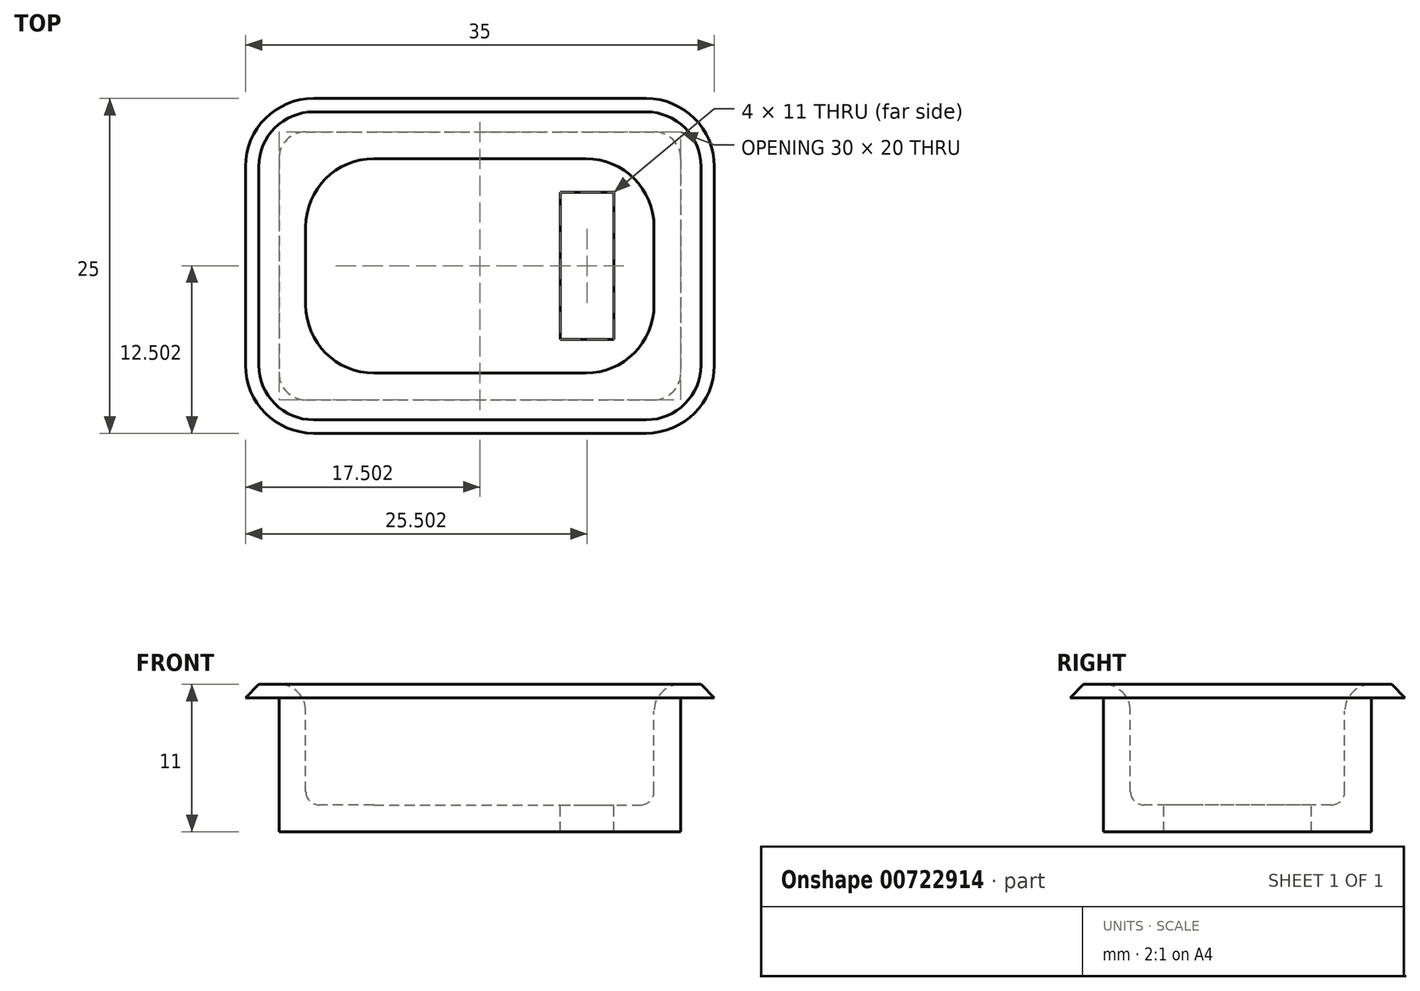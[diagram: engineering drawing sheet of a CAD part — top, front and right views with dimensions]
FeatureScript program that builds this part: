
annotation { "Feature Type Name" : "Feature", "Feature Type Description" : "" }
export const myFeature = defineFeature(function(context is Context, id is Id, definition is map)
    precondition{}
    {
        {
            var Q0;
            Q0=qCreatedBy(makeId("Top.planeOp"),FACE);
            var sketch = newSketch(context, id + "F0", { "sketchPlane" : qUnion([Q0])});
            skLineSegment(sketch, "E0.bottom", {"start": v(-34.97, -17.82) * mm, "end": v(-4.97, -17.82) * mm});
            skLineSegment(sketch, "E0.top", {"start": v(-34.97, -37.82) * mm, "end": v(-4.97, -37.82) * mm});
            skLineSegment(sketch, "E0.left", {"start": v(-34.97, -17.82) * mm, "end": v(-34.97, -37.82) * mm});
            skLineSegment(sketch, "E0.right", {"start": v(-4.97, -17.82) * mm, "end": v(-4.97, -37.82) * mm});
            skSolve(sketch);
        }
        {
            var Q0;
            Q0=makeQuery(id+"F0.imprint","IMPRINT",FACE,{"disambiguationData":[TD([[makeQuery(id+"F0.imprint","IMPRINT",EDGE,{"derivedFrom":sQuery(id+"F0.wireOp",EDGE,"E0.bottom")}),-1.0]])]});
            extrude(context, id + "F1", {"entities" : qUnion([Q0]), "depth" : 10 * mm, "offsetDistance" : 25.4 * mm});
        }
        {
            var Q0;
            Q0=makeQuery(id+"F1.opExtrude","SWEPT_EDGE",EDGE,{"disambiguationData":[OSD([sQuery(id+"F0.wireOp",EDGE,"E0.top"),sQuery(id+"F0.wireOp",EDGE,"E0.right")])]});
            var Q1;
            Q1=makeQuery(id+"F1.opExtrude","SWEPT_EDGE",EDGE,{"disambiguationData":[OSD([sQuery(id+"F0.wireOp",EDGE,"E0.bottom"),sQuery(id+"F0.wireOp",EDGE,"E0.right")])]});
            var Q2;
            Q2=makeQuery(id+"F1.opExtrude","SWEPT_EDGE",EDGE,{"disambiguationData":[OSD([sQuery(id+"F0.wireOp",EDGE,"E0.top"),sQuery(id+"F0.wireOp",EDGE,"E0.left")])]});
            var Q3;
            Q3=makeQuery(id+"F1.opExtrude","SWEPT_EDGE",EDGE,{"disambiguationData":[OSD([sQuery(id+"F0.wireOp",EDGE,"E0.bottom"),sQuery(id+"F0.wireOp",EDGE,"E0.left")])]});
            fillet(context, id + "F2", {"entities" : qUnion([Q0, Q1, Q2, Q3]), "radius" : 2 * mm, "tangentPropagation" : true, "allowEdgeOverflow" : false});
        }
        {
            var Q0;
            Q0=makeQuery(id+"F1.opExtrude","CAP_FACE",FACE,{"disambiguationData":[OSD([sQuery(id+"F0.wireOp",EDGE,"E0.bottom"),sQuery(id+"F0.wireOp",EDGE,"E0.top"),sQuery(id+"F0.wireOp",EDGE,"E0.left"),sQuery(id+"F0.wireOp",EDGE,"E0.right")])],"isStart":false});
            shell(context, id + "F3", {"entities" : qUnion([Q0]), "thickness" : 2 * mm});
        }
        {
            var Q0;
            Q0=makeQuery(id+"F3.opShell","OFFSET_FACE",FACE,{"disambiguationData":[OSD([sQuery(id+"F0.wireOp",EDGE,"E0.bottom"),sQuery(id+"F0.wireOp",EDGE,"E0.top"),sQuery(id+"F0.wireOp",EDGE,"E0.left"),sQuery(id+"F0.wireOp",EDGE,"E0.right")])]});
            var sketch = newSketch(context, id + "F4", { "sketchPlane" : qUnion([Q0])});
            skLineSegment(sketch, "E1.bottom", {"start": v(-13.97, -22.32) * mm, "end": v(-9.97, -22.32) * mm});
            skLineSegment(sketch, "E1.top", {"start": v(-13.97, -33.32) * mm, "end": v(-9.97, -33.32) * mm});
            skLineSegment(sketch, "E1.left", {"start": v(-13.97, -22.32) * mm, "end": v(-13.97, -33.32) * mm});
            skLineSegment(sketch, "E1.right", {"start": v(-9.97, -22.32) * mm, "end": v(-9.97, -33.32) * mm});
            skSolve(sketch);
        }
        {
            var Q0;
            Q0=makeQuery(id+"F4.imprint","IMPRINT",FACE,{"disambiguationData":[TD([[makeQuery(id+"F4.imprint","IMPRINT",EDGE,{"derivedFrom":sQuery(id+"F4.wireOp",EDGE,"E1.bottom")}),-1.0]])]});
            extrude(context, id + "F5", {"entities" : qUnion([Q0]), "operationType" : NewBodyOperationType.REMOVE, "endBound" : BoundingType.THROUGH_ALL, "oppositeDirection" : true, "depth" : 25.4 * mm, "offsetDistance" : 25.4 * mm});
        }
        {
            var Q0;
            Q0=makeQuery(id+"F1.opExtrude","CAP_FACE",FACE,{"disambiguationData":[OSD([sQuery(id+"F0.wireOp",EDGE,"E0.bottom"),sQuery(id+"F0.wireOp",EDGE,"E0.top"),sQuery(id+"F0.wireOp",EDGE,"E0.left"),sQuery(id+"F0.wireOp",EDGE,"E0.right")])],"isStart":false});
            var sketch = newSketch(context, id + "F6", { "sketchPlane" : qUnion([Q0])});
            skLineSegment(sketch, "E2.bottom", {"start": v(-32.97, -19.82) * mm, "end": v(-6.97, -19.82) * mm});
            skLineSegment(sketch, "E2.top", {"start": v(-32.97, -35.82) * mm, "end": v(-6.97, -35.82) * mm});
            skLineSegment(sketch, "E2.left", {"start": v(-32.97, -19.82) * mm, "end": v(-32.97, -35.82) * mm});
            skLineSegment(sketch, "E2.right", {"start": v(-6.97, -19.82) * mm, "end": v(-6.97, -35.82) * mm});
            skLineSegment(sketch, "E3.bottom", {"start": v(-37.47, -15.32) * mm, "end": v(-2.47, -15.32) * mm});
            skLineSegment(sketch, "E3.top", {"start": v(-37.47, -40.32) * mm, "end": v(-2.47, -40.32) * mm});
            skLineSegment(sketch, "E3.left", {"start": v(-37.47, -15.32) * mm, "end": v(-37.47, -40.32) * mm});
            skLineSegment(sketch, "E3.right", {"start": v(-2.47, -15.32) * mm, "end": v(-2.47, -40.32) * mm});
            skSolve(sketch);
        }
        {
            var Q0;
            Q0=makeQuery(id+"F6.imprint","IMPRINT",FACE,{"disambiguationData":[TD([[makeQuery(id+"F6.imprint","IMPRINT",EDGE,{"derivedFrom":sQuery(id+"F6.wireOp",EDGE,"E3.bottom")}),-1.0]])]});
            var Q1;
            Q1=makeQuery(id+"F6.imprint","IMPRINT",FACE,{"disambiguationData":[TD([[makeQuery(id+"F6.imprint","IMPRINT",EDGE,{"derivedFrom":sQuery(id+"F6.wireOp",EDGE,"E2.bottom")}),1.0]])]});
            extrude(context, id + "F7", {"entities" : qUnion([Q0, Q1]), "operationType" : NewBodyOperationType.ADD, "depth" : 1 * mm, "offsetDistance" : 25.4 * mm});
        }
        {
            var Q0;
            Q0=makeQuery(id+"F7.opExtrude","SWEPT_EDGE",EDGE,{"disambiguationData":[OSD([sQuery(id+"F6.wireOp",EDGE,"E3.top"),sQuery(id+"F6.wireOp",EDGE,"E3.right")])]});
            var Q1;
            Q1=makeQuery(id+"F7.opExtrude","SWEPT_EDGE",EDGE,{"disambiguationData":[OSD([sQuery(id+"F6.wireOp",EDGE,"E3.top"),sQuery(id+"F6.wireOp",EDGE,"E3.left")])]});
            var Q2;
            Q2=makeQuery(id+"F7.opExtrude","SWEPT_EDGE",EDGE,{"disambiguationData":[OSD([sQuery(id+"F6.wireOp",EDGE,"E3.bottom"),sQuery(id+"F6.wireOp",EDGE,"E3.right")])]});
            var Q3;
            Q3=makeQuery(id+"F7.opExtrude","SWEPT_EDGE",EDGE,{"disambiguationData":[OSD([sQuery(id+"F6.wireOp",EDGE,"E3.bottom"),sQuery(id+"F6.wireOp",EDGE,"E3.left")])]});
            fillet(context, id + "F8", {"entities" : qUnion([Q0, Q1, Q2, Q3]), "radius" : 5.08 * mm, "tangentPropagation" : true, "allowEdgeOverflow" : false});
        }
        {
            var Q0;
            Q0=makeQuery(id+"F7.boolean.opBoolean","MERGE",EDGE,{"derivedFrom":[makeQuery(id+"F3.opShell","OFFSET_EDGE",EDGE,{"disambiguationData":[OSD([sQuery(id+"F0.wireOp",EDGE,"E0.top"),sQuery(id+"F0.wireOp",EDGE,"E0.right")])]}),makeQuery(id+"F7.opExtrude","SWEPT_EDGE",EDGE,{"disambiguationData":[OSD([sQuery(id+"F6.wireOp",EDGE,"E2.top"),sQuery(id+"F6.wireOp",EDGE,"E2.right")])]})]});
            var Q1;
            Q1=makeQuery(id+"F7.boolean.opBoolean","MERGE",EDGE,{"derivedFrom":[makeQuery(id+"F3.opShell","OFFSET_EDGE",EDGE,{"disambiguationData":[OSD([sQuery(id+"F0.wireOp",EDGE,"E0.bottom"),sQuery(id+"F0.wireOp",EDGE,"E0.right")])]}),makeQuery(id+"F7.opExtrude","SWEPT_EDGE",EDGE,{"disambiguationData":[OSD([sQuery(id+"F6.wireOp",EDGE,"E2.bottom"),sQuery(id+"F6.wireOp",EDGE,"E2.right")])]})]});
            var Q2;
            Q2=makeQuery(id+"F7.boolean.opBoolean","MERGE",EDGE,{"derivedFrom":[makeQuery(id+"F3.opShell","OFFSET_EDGE",EDGE,{"disambiguationData":[OSD([sQuery(id+"F0.wireOp",EDGE,"E0.bottom"),sQuery(id+"F0.wireOp",EDGE,"E0.left")])]}),makeQuery(id+"F7.opExtrude","SWEPT_EDGE",EDGE,{"disambiguationData":[OSD([sQuery(id+"F6.wireOp",EDGE,"E2.bottom"),sQuery(id+"F6.wireOp",EDGE,"E2.left")])]})]});
            var Q3;
            Q3=makeQuery(id+"F7.boolean.opBoolean","MERGE",EDGE,{"derivedFrom":[makeQuery(id+"F3.opShell","OFFSET_EDGE",EDGE,{"disambiguationData":[OSD([sQuery(id+"F0.wireOp",EDGE,"E0.top"),sQuery(id+"F0.wireOp",EDGE,"E0.left")])]}),makeQuery(id+"F7.opExtrude","SWEPT_EDGE",EDGE,{"disambiguationData":[OSD([sQuery(id+"F6.wireOp",EDGE,"E2.top"),sQuery(id+"F6.wireOp",EDGE,"E2.left")])]})]});
            fillet(context, id + "F9", {"entities" : qUnion([Q0, Q1, Q2, Q3]), "radius" : 5.08 * mm, "tangentPropagation" : true, "allowEdgeOverflow" : false});
        }
        {
            var Q0;
            {var subQ0=sQuery(id+"F0.wireOp",EDGE,"E0.bottom");Q0=makeQuery(id+"F3.opShell","OFFSET_EDGE",EDGE,{"disambiguationData":[OSD([subQ0]),TDD([makeQuery(id+"F1.opExtrude","CAP_EDGE",EDGE,{"disambiguationData":[OSD([subQ0])],"isStart":true})])]});}
            fillet(context, id + "F10", {"entities" : qUnion([Q0]), "radius" : 1 * mm, "tangentPropagation" : true, "allowEdgeOverflow" : false});
        }
        {
            var Q0;
            Q0=makeQuery(id+"F7.opExtrude","CAP_EDGE",EDGE,{"disambiguationData":[OSD([sQuery(id+"F6.wireOp",EDGE,"E2.bottom")])],"isStart":false});
            var Q1;
            {var subQ0=sQuery(id+"F6.wireOp",EDGE,"E2.left");var subQ1=sQuery(id+"F6.wireOp",EDGE,"E2.bottom");Q1=makeQuery(id+"F9.opFillet","BLEND_EDGE",EDGE,{"blendedFrom":[makeQuery(id+"F7.boolean.opBoolean","MERGE",EDGE,{"derivedFrom":[makeQuery(id+"F3.opShell","OFFSET_EDGE",EDGE,{"disambiguationData":[OSD([sQuery(id+"F0.wireOp",EDGE,"E0.bottom"),sQuery(id+"F0.wireOp",EDGE,"E0.left")])]}),makeQuery(id+"F7.opExtrude","SWEPT_EDGE",EDGE,{"disambiguationData":[OSD([subQ1,subQ0])]})]}),makeQuery(id+"F7.opExtrude","CAP_FACE",FACE,{"disambiguationData":[OSD([subQ1,sQuery(id+"F6.wireOp",EDGE,"E2.top"),subQ0,sQuery(id+"F6.wireOp",EDGE,"E2.right"),sQuery(id+"F6.wireOp",EDGE,"E3.bottom"),sQuery(id+"F6.wireOp",EDGE,"E3.top"),sQuery(id+"F6.wireOp",EDGE,"E3.left"),sQuery(id+"F6.wireOp",EDGE,"E3.right")])],"isStart":false})],"blendedInto":[makeQuery(id+"F7.opExtrude","CAP_FACE",FACE,{"disambiguationData":[OSD([subQ1,sQuery(id+"F6.wireOp",EDGE,"E2.top"),subQ0,sQuery(id+"F6.wireOp",EDGE,"E2.right"),sQuery(id+"F6.wireOp",EDGE,"E3.bottom"),sQuery(id+"F6.wireOp",EDGE,"E3.top"),sQuery(id+"F6.wireOp",EDGE,"E3.left"),sQuery(id+"F6.wireOp",EDGE,"E3.right")])],"isStart":false})]});}
            var Q2;
            Q2=makeQuery(id+"F7.opExtrude","CAP_EDGE",EDGE,{"disambiguationData":[OSD([sQuery(id+"F6.wireOp",EDGE,"E2.left")])],"isStart":false});
            var Q3;
            {var subQ0=sQuery(id+"F6.wireOp",EDGE,"E2.left");var subQ1=sQuery(id+"F6.wireOp",EDGE,"E2.top");Q3=makeQuery(id+"F9.opFillet","BLEND_EDGE",EDGE,{"blendedFrom":[makeQuery(id+"F7.boolean.opBoolean","MERGE",EDGE,{"derivedFrom":[makeQuery(id+"F3.opShell","OFFSET_EDGE",EDGE,{"disambiguationData":[OSD([sQuery(id+"F0.wireOp",EDGE,"E0.top"),sQuery(id+"F0.wireOp",EDGE,"E0.left")])]}),makeQuery(id+"F7.opExtrude","SWEPT_EDGE",EDGE,{"disambiguationData":[OSD([subQ1,subQ0])]})]}),makeQuery(id+"F7.opExtrude","CAP_FACE",FACE,{"disambiguationData":[OSD([sQuery(id+"F6.wireOp",EDGE,"E2.bottom"),subQ1,subQ0,sQuery(id+"F6.wireOp",EDGE,"E2.right"),sQuery(id+"F6.wireOp",EDGE,"E3.bottom"),sQuery(id+"F6.wireOp",EDGE,"E3.top"),sQuery(id+"F6.wireOp",EDGE,"E3.left"),sQuery(id+"F6.wireOp",EDGE,"E3.right")])],"isStart":false})],"blendedInto":[makeQuery(id+"F7.opExtrude","CAP_FACE",FACE,{"disambiguationData":[OSD([sQuery(id+"F6.wireOp",EDGE,"E2.bottom"),subQ1,subQ0,sQuery(id+"F6.wireOp",EDGE,"E2.right"),sQuery(id+"F6.wireOp",EDGE,"E3.bottom"),sQuery(id+"F6.wireOp",EDGE,"E3.top"),sQuery(id+"F6.wireOp",EDGE,"E3.left"),sQuery(id+"F6.wireOp",EDGE,"E3.right")])],"isStart":false})]});}
            var Q4;
            Q4=makeQuery(id+"F7.opExtrude","CAP_EDGE",EDGE,{"disambiguationData":[OSD([sQuery(id+"F6.wireOp",EDGE,"E2.top")])],"isStart":false});
            var Q5;
            {var subQ0=sQuery(id+"F6.wireOp",EDGE,"E2.right");var subQ1=sQuery(id+"F6.wireOp",EDGE,"E2.top");Q5=makeQuery(id+"F9.opFillet","BLEND_EDGE",EDGE,{"blendedFrom":[makeQuery(id+"F7.boolean.opBoolean","MERGE",EDGE,{"derivedFrom":[makeQuery(id+"F3.opShell","OFFSET_EDGE",EDGE,{"disambiguationData":[OSD([sQuery(id+"F0.wireOp",EDGE,"E0.top"),sQuery(id+"F0.wireOp",EDGE,"E0.right")])]}),makeQuery(id+"F7.opExtrude","SWEPT_EDGE",EDGE,{"disambiguationData":[OSD([subQ1,subQ0])]})]}),makeQuery(id+"F7.opExtrude","CAP_FACE",FACE,{"disambiguationData":[OSD([sQuery(id+"F6.wireOp",EDGE,"E2.bottom"),subQ1,sQuery(id+"F6.wireOp",EDGE,"E2.left"),subQ0,sQuery(id+"F6.wireOp",EDGE,"E3.bottom"),sQuery(id+"F6.wireOp",EDGE,"E3.top"),sQuery(id+"F6.wireOp",EDGE,"E3.left"),sQuery(id+"F6.wireOp",EDGE,"E3.right")])],"isStart":false})],"blendedInto":[makeQuery(id+"F7.opExtrude","CAP_FACE",FACE,{"disambiguationData":[OSD([sQuery(id+"F6.wireOp",EDGE,"E2.bottom"),subQ1,sQuery(id+"F6.wireOp",EDGE,"E2.left"),subQ0,sQuery(id+"F6.wireOp",EDGE,"E3.bottom"),sQuery(id+"F6.wireOp",EDGE,"E3.top"),sQuery(id+"F6.wireOp",EDGE,"E3.left"),sQuery(id+"F6.wireOp",EDGE,"E3.right")])],"isStart":false})]});}
            var Q6;
            Q6=makeQuery(id+"F7.opExtrude","CAP_EDGE",EDGE,{"disambiguationData":[OSD([sQuery(id+"F6.wireOp",EDGE,"E2.right")])],"isStart":false});
            var Q7;
            {var subQ0=sQuery(id+"F6.wireOp",EDGE,"E2.right");var subQ1=sQuery(id+"F6.wireOp",EDGE,"E2.bottom");Q7=makeQuery(id+"F9.opFillet","BLEND_EDGE",EDGE,{"blendedFrom":[makeQuery(id+"F7.boolean.opBoolean","MERGE",EDGE,{"derivedFrom":[makeQuery(id+"F3.opShell","OFFSET_EDGE",EDGE,{"disambiguationData":[OSD([sQuery(id+"F0.wireOp",EDGE,"E0.bottom"),sQuery(id+"F0.wireOp",EDGE,"E0.right")])]}),makeQuery(id+"F7.opExtrude","SWEPT_EDGE",EDGE,{"disambiguationData":[OSD([subQ1,subQ0])]})]}),makeQuery(id+"F7.opExtrude","CAP_FACE",FACE,{"disambiguationData":[OSD([subQ1,sQuery(id+"F6.wireOp",EDGE,"E2.top"),sQuery(id+"F6.wireOp",EDGE,"E2.left"),subQ0,sQuery(id+"F6.wireOp",EDGE,"E3.bottom"),sQuery(id+"F6.wireOp",EDGE,"E3.top"),sQuery(id+"F6.wireOp",EDGE,"E3.left"),sQuery(id+"F6.wireOp",EDGE,"E3.right")])],"isStart":false})],"blendedInto":[makeQuery(id+"F7.opExtrude","CAP_FACE",FACE,{"disambiguationData":[OSD([subQ1,sQuery(id+"F6.wireOp",EDGE,"E2.top"),sQuery(id+"F6.wireOp",EDGE,"E2.left"),subQ0,sQuery(id+"F6.wireOp",EDGE,"E3.bottom"),sQuery(id+"F6.wireOp",EDGE,"E3.top"),sQuery(id+"F6.wireOp",EDGE,"E3.left"),sQuery(id+"F6.wireOp",EDGE,"E3.right")])],"isStart":false})]});}
            fillet(context, id + "F11", {"entities" : qUnion([Q0, Q1, Q2, Q3, Q4, Q5, Q6, Q7]), "radius" : 2 * mm, "tangentPropagation" : true, "allowEdgeOverflow" : false});
        }
        {
            var Q0;
            Q0=makeQuery(id+"F7.opExtrude","CAP_EDGE",EDGE,{"disambiguationData":[OSD([sQuery(id+"F6.wireOp",EDGE,"E3.top")])],"isStart":false});
            var Q1;
            {var subQ0=sQuery(id+"F6.wireOp",EDGE,"E3.left");var subQ1=sQuery(id+"F6.wireOp",EDGE,"E3.top");Q1=makeQuery(id+"F8.opFillet","BLEND_EDGE",EDGE,{"blendedFrom":[makeQuery(id+"F7.opExtrude","SWEPT_EDGE",EDGE,{"disambiguationData":[OSD([subQ1,subQ0])]}),makeQuery(id+"F7.opExtrude","CAP_FACE",FACE,{"disambiguationData":[OSD([sQuery(id+"F6.wireOp",EDGE,"E2.bottom"),sQuery(id+"F6.wireOp",EDGE,"E2.top"),sQuery(id+"F6.wireOp",EDGE,"E2.left"),sQuery(id+"F6.wireOp",EDGE,"E2.right"),sQuery(id+"F6.wireOp",EDGE,"E3.bottom"),subQ1,subQ0,sQuery(id+"F6.wireOp",EDGE,"E3.right")])],"isStart":false})],"blendedInto":[makeQuery(id+"F7.opExtrude","CAP_FACE",FACE,{"disambiguationData":[OSD([sQuery(id+"F6.wireOp",EDGE,"E2.bottom"),sQuery(id+"F6.wireOp",EDGE,"E2.top"),sQuery(id+"F6.wireOp",EDGE,"E2.left"),sQuery(id+"F6.wireOp",EDGE,"E2.right"),sQuery(id+"F6.wireOp",EDGE,"E3.bottom"),subQ1,subQ0,sQuery(id+"F6.wireOp",EDGE,"E3.right")])],"isStart":false})]});}
            var Q2;
            Q2=makeQuery(id+"F7.opExtrude","CAP_EDGE",EDGE,{"disambiguationData":[OSD([sQuery(id+"F6.wireOp",EDGE,"E3.left")])],"isStart":false});
            var Q3;
            {var subQ0=sQuery(id+"F6.wireOp",EDGE,"E3.left");var subQ1=sQuery(id+"F6.wireOp",EDGE,"E3.bottom");Q3=makeQuery(id+"F8.opFillet","BLEND_EDGE",EDGE,{"blendedFrom":[makeQuery(id+"F7.opExtrude","SWEPT_EDGE",EDGE,{"disambiguationData":[OSD([subQ1,subQ0])]}),makeQuery(id+"F7.opExtrude","CAP_FACE",FACE,{"disambiguationData":[OSD([sQuery(id+"F6.wireOp",EDGE,"E2.bottom"),sQuery(id+"F6.wireOp",EDGE,"E2.top"),sQuery(id+"F6.wireOp",EDGE,"E2.left"),sQuery(id+"F6.wireOp",EDGE,"E2.right"),subQ1,sQuery(id+"F6.wireOp",EDGE,"E3.top"),subQ0,sQuery(id+"F6.wireOp",EDGE,"E3.right")])],"isStart":false})],"blendedInto":[makeQuery(id+"F7.opExtrude","CAP_FACE",FACE,{"disambiguationData":[OSD([sQuery(id+"F6.wireOp",EDGE,"E2.bottom"),sQuery(id+"F6.wireOp",EDGE,"E2.top"),sQuery(id+"F6.wireOp",EDGE,"E2.left"),sQuery(id+"F6.wireOp",EDGE,"E2.right"),subQ1,sQuery(id+"F6.wireOp",EDGE,"E3.top"),subQ0,sQuery(id+"F6.wireOp",EDGE,"E3.right")])],"isStart":false})]});}
            var Q4;
            Q4=makeQuery(id+"F7.opExtrude","CAP_EDGE",EDGE,{"disambiguationData":[OSD([sQuery(id+"F6.wireOp",EDGE,"E3.bottom")])],"isStart":false});
            var Q5;
            {var subQ0=sQuery(id+"F6.wireOp",EDGE,"E3.right");var subQ1=sQuery(id+"F6.wireOp",EDGE,"E3.top");Q5=makeQuery(id+"F8.opFillet","BLEND_EDGE",EDGE,{"blendedFrom":[makeQuery(id+"F7.opExtrude","SWEPT_EDGE",EDGE,{"disambiguationData":[OSD([subQ1,subQ0])]}),makeQuery(id+"F7.opExtrude","CAP_FACE",FACE,{"disambiguationData":[OSD([sQuery(id+"F6.wireOp",EDGE,"E2.bottom"),sQuery(id+"F6.wireOp",EDGE,"E2.top"),sQuery(id+"F6.wireOp",EDGE,"E2.left"),sQuery(id+"F6.wireOp",EDGE,"E2.right"),sQuery(id+"F6.wireOp",EDGE,"E3.bottom"),subQ1,sQuery(id+"F6.wireOp",EDGE,"E3.left"),subQ0])],"isStart":false})],"blendedInto":[makeQuery(id+"F7.opExtrude","CAP_FACE",FACE,{"disambiguationData":[OSD([sQuery(id+"F6.wireOp",EDGE,"E2.bottom"),sQuery(id+"F6.wireOp",EDGE,"E2.top"),sQuery(id+"F6.wireOp",EDGE,"E2.left"),sQuery(id+"F6.wireOp",EDGE,"E2.right"),sQuery(id+"F6.wireOp",EDGE,"E3.bottom"),subQ1,sQuery(id+"F6.wireOp",EDGE,"E3.left"),subQ0])],"isStart":false})]});}
            var Q6;
            Q6=makeQuery(id+"F7.opExtrude","CAP_EDGE",EDGE,{"disambiguationData":[OSD([sQuery(id+"F6.wireOp",EDGE,"E3.right")])],"isStart":false});
            chamfer(context, id + "F12", {"entities" : qUnion([Q0, Q1, Q2, Q3, Q4, Q5, Q6]), "width" : 1 * mm, "tangentPropagation" : true});
        }
    });
